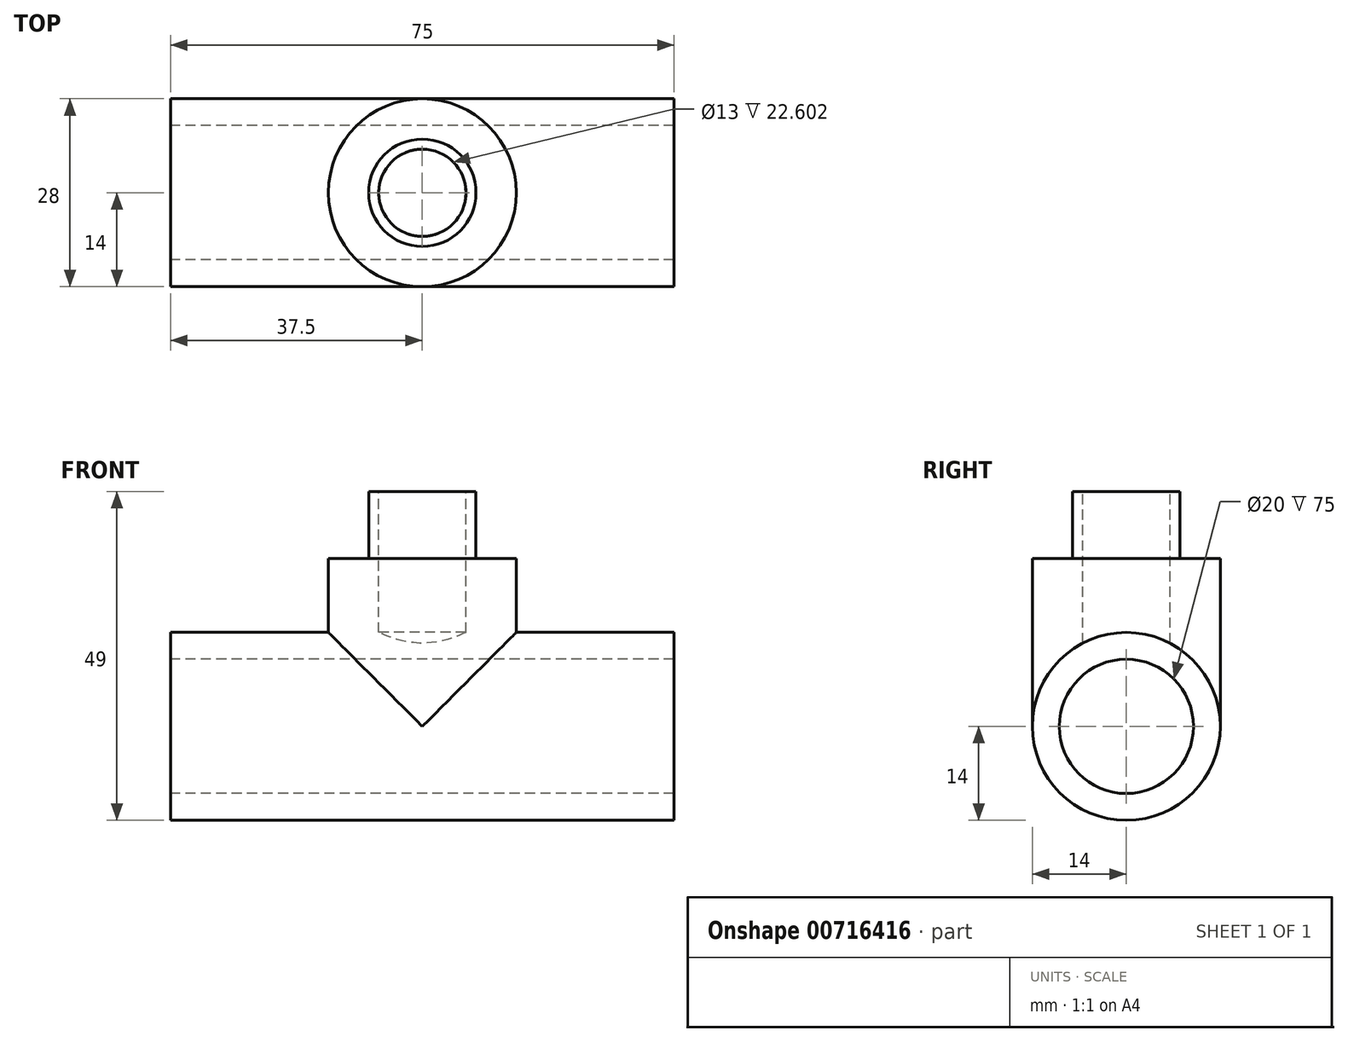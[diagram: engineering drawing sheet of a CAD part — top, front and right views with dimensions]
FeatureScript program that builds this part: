
annotation { "Feature Type Name" : "Feature", "Feature Type Description" : "" }
export const myFeature = defineFeature(function(context is Context, id is Id, definition is map)
    precondition{}
    {
        {
            var Q0;
            Q0=qCreatedBy(makeId("Top.planeOp"),FACE);
            var sketch = newSketch(context, id + "F0", { "sketchPlane" : qUnion([Q0])});
            skLineSegment(sketch, "E0", {"start": v(-59.15, 0) * mm, "end": v(57.24, 0) * mm, "construction": true});
            skLineSegment(sketch, "E1.bottom", {"start": v(-25, 14) * mm, "end": v(50, 14) * mm});
            skLineSegment(sketch, "E1.top", {"start": v(-25, 10) * mm, "end": v(50, 10) * mm});
            skLineSegment(sketch, "E1.left", {"start": v(-25, 14) * mm, "end": v(-25, 10) * mm});
            skLineSegment(sketch, "E1.right", {"start": v(50, 14) * mm, "end": v(50, 10) * mm});
            skSolve(sketch);
        }
        {
            var Q0;
            Q0=qSketchRegion(id+"F0",true);
            var Q1;
            Q1=sQuery(id+"F0.wireOp",EDGE,"E0");
            revolve(context, id + "F1", {"surfaceOperationType" : NewSurfaceOperationType.NEW, "entities" : qUnion([Q0]), "axis" : qUnion([Q1]), "revolveType" : RevolveType.FULL});
        }
        {
            var Q0;
            Q0=qCreatedBy(makeId("Front.planeOp"),FACE);
            var sketch = newSketch(context, id + "F2", { "sketchPlane" : qUnion([Q0])});
            skLineSegment(sketch, "E2", {"start": v(12.5, 36.45) * mm, "end": v(12.5, -50.55) * mm, "construction": true});
            skLineSegment(sketch, "E3", {"start": v(-1.5, 0) * mm, "end": v(-1.5, 25) * mm});
            skLineSegment(sketch, "E4", {"start": v(-1.5, 25) * mm, "end": v(4.5, 25) * mm});
            skLineSegment(sketch, "E5", {"start": v(4.5, 25) * mm, "end": v(4.5, 35) * mm});
            skLineSegment(sketch, "E6", {"start": v(4.5, 35) * mm, "end": v(6, 35) * mm});
            skLineSegment(sketch, "E7", {"start": v(6, 35) * mm, "end": v(6, 0) * mm});
            skLineSegment(sketch, "E8", {"start": v(6, 0) * mm, "end": v(-1.5, 0) * mm});
            skSolve(sketch);
        }
        {
            var Q0;
            Q0=qSketchRegion(id+"F2",true);
            var Q1;
            Q1=sQuery(id+"F2.wireOp",EDGE,"E2");
            revolve(context, id + "F3", {"operationType" : NewBodyOperationType.ADD, "surfaceOperationType" : NewSurfaceOperationType.NEW, "entities" : qUnion([Q0]), "axis" : qUnion([Q1]), "revolveType" : RevolveType.FULL});
        }
        {
            var Q0;
            Q0=makeQuery(id+"F1.opRevolve","SWEPT_FACE",FACE,{"disambiguationData":[OSD([sQuery(id+"F0.wireOp",EDGE,"E1.right")])]});
            var sketch = newSketch(context, id + "F4", { "sketchPlane" : qUnion([Q0])});
            skCircle(sketch, "E9", {"center": v(0, 0) * mm, "radius": 10 * mm});
            skSolve(sketch);
        }
        {
            var Q0;
            Q0 = qSketchRegion(id + "F4", true);
            extrude(context, id + "F5", {"entities" : qUnion([Q0]), "operationType" : NewBodyOperationType.REMOVE, "endBound" : BoundingType.THROUGH_ALL, "oppositeDirection" : true, "depth" : 25 * mm, "offsetDistance" : 25 * mm});
        }
    });
